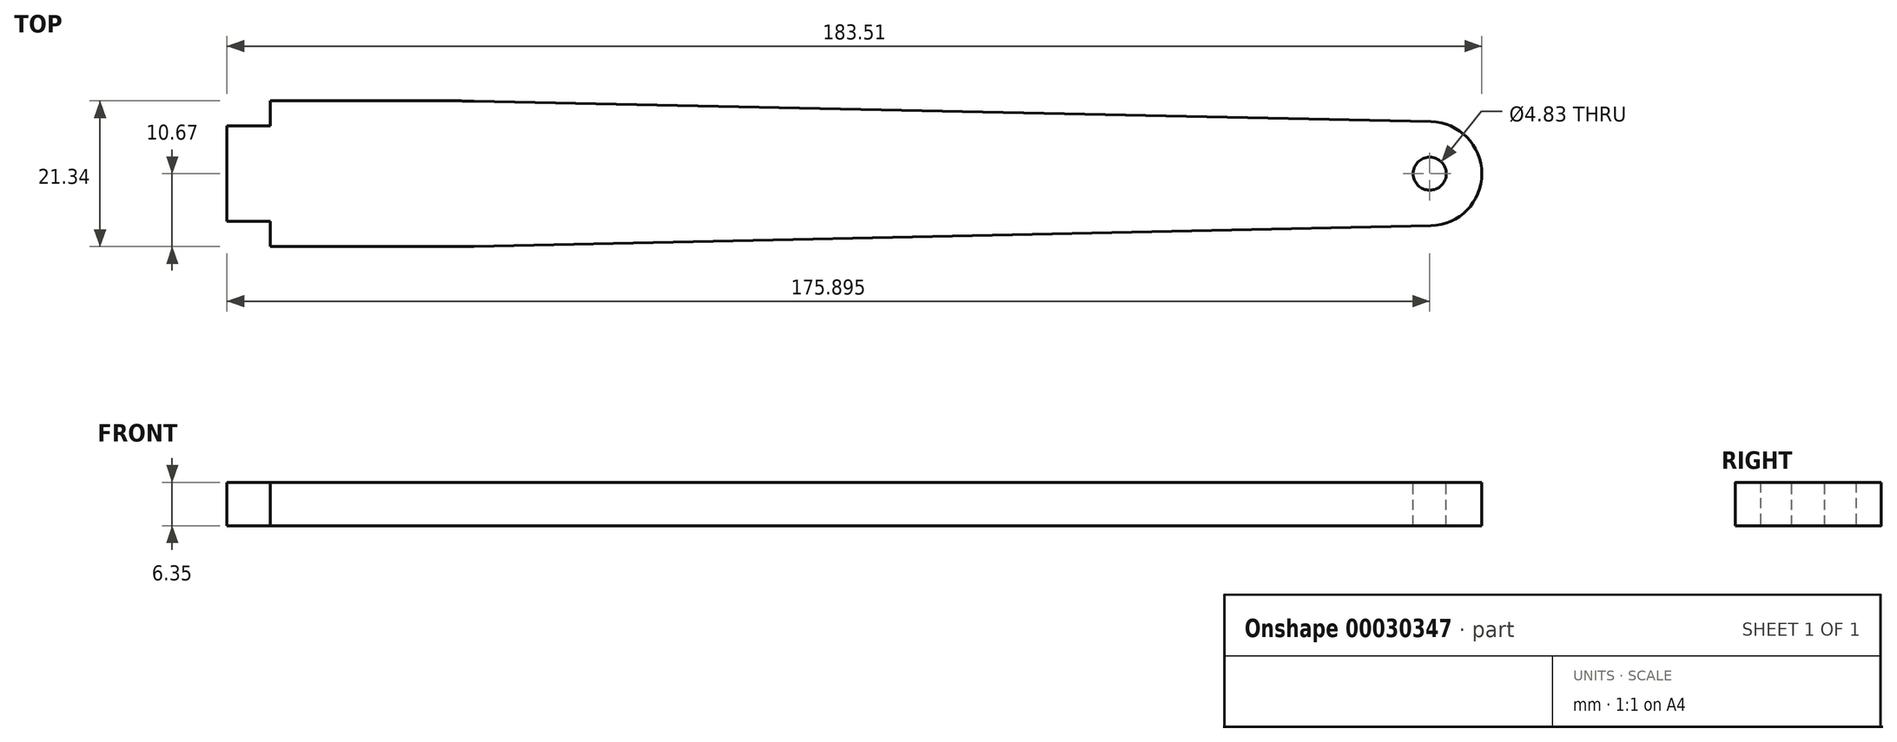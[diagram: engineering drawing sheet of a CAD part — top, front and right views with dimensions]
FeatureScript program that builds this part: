
annotation { "Feature Type Name" : "Feature", "Feature Type Description" : "" }
export const myFeature = defineFeature(function(context is Context, id is Id, definition is map)
    precondition{}
    {
        {
            var Q0;
            Q0=qCreatedBy(makeId("Top.planeOp"),FACE);
            var sketch = newSketch(context, id + "F0", { "sketchPlane" : qUnion([Q0])});
            skLineSegment(sketch, "E0", {"start": v(-6.35, 0) * mm, "end": v(-6.35, 6.99) * mm});
            skLineSegment(sketch, "E1", {"start": v(-6.35, 6.99) * mm, "end": v(0, 6.99) * mm});
            skLineSegment(sketch, "E2", {"start": v(0, 6.99) * mm, "end": v(0, 10.67) * mm});
            skLineSegment(sketch, "E3", {"start": v(0, 10.67) * mm, "end": v(25.4, 10.67) * mm});
            skLineSegment(sketch, "E4", {"start": v(29.76, 10.62) * mm, "end": v(169.7, 7.62) * mm});
            skArc(sketch, "E5", {"start": v(169.7, 7.62) * mm, "mid": v(175, 5.33) * mm, "end": v(177.16, 0) * mm});
            skPoint(sketch, "E6.visualSharp", {"position": v(27.58, 10.67) * mm});
            skArc(sketch, "E6.filletArc", {"start": v(29.76, 10.62) * mm, "mid": v(27.58, 10.66) * mm, "end": v(25.4, 10.67) * mm});
            skArc(sketch, "E7.MirrorCS", {"start": v(169.7, -7.62) * mm, "mid": v(175, -5.33) * mm, "end": v(177.16, 0) * mm});
            skLineSegment(sketch, "E8.MirrorCS", {"start": v(29.76, -10.62) * mm, "end": v(169.7, -7.62) * mm});
            skArc(sketch, "E9.MirrorCS", {"start": v(29.76, -10.62) * mm, "mid": v(27.58, -10.66) * mm, "end": v(25.4, -10.67) * mm});
            skLineSegment(sketch, "E10.MirrorCS", {"start": v(0, -10.67) * mm, "end": v(25.4, -10.67) * mm});
            skLineSegment(sketch, "E11.MirrorCS", {"start": v(0, -6.99) * mm, "end": v(0, -10.67) * mm});
            skLineSegment(sketch, "E12.MirrorCS", {"start": v(-6.35, 0) * mm, "end": v(-6.35, -6.99) * mm});
            skLineSegment(sketch, "E13.MirrorCS", {"start": v(-6.35, -6.99) * mm, "end": v(0, -6.99) * mm});
            skSolve(sketch);
        }
        {
            var Q0;
            Q0 = qSketchRegion(id + "F0", true);
            extrude(context, id + "F1", {"entities" : qUnion([Q0]), "depth" : 6.35 * mm});
        }
        {
            var Q0;
            Q0=makeQuery(id+"F1.opExtrude","CAP_FACE",FACE,{"disambiguationData":[OSD([sQuery(id+"F0.wireOp",EDGE,"E0"),sQuery(id+"F0.wireOp",EDGE,"E1"),sQuery(id+"F0.wireOp",EDGE,"E2"),sQuery(id+"F0.wireOp",EDGE,"E3"),sQuery(id+"F0.wireOp",EDGE,"E4"),sQuery(id+"F0.wireOp",EDGE,"E5"),sQuery(id+"F0.wireOp",EDGE,"E6.filletArc"),sQuery(id+"F0.wireOp",EDGE,"E7.MirrorCS"),sQuery(id+"F0.wireOp",EDGE,"E8.MirrorCS"),sQuery(id+"F0.wireOp",EDGE,"E9.MirrorCS"),sQuery(id+"F0.wireOp",EDGE,"E10.MirrorCS"),sQuery(id+"F0.wireOp",EDGE,"E11.MirrorCS"),sQuery(id+"F0.wireOp",EDGE,"E12.MirrorCS"),sQuery(id+"F0.wireOp",EDGE,"E13.MirrorCS")])],"isStart":false});
            var sketch = newSketch(context, id + "F2", { "sketchPlane" : qUnion([Q0])});
            skCircle(sketch, "E14", {"center": v(169.54, 0) * mm, "radius": 2.41 * mm});
            skSolve(sketch);
        }
        {
            var Q0;
            Q0 = qSketchRegion(id + "F2", true);
            extrude(context, id + "F3", {"entities" : qUnion([Q0]), "operationType" : NewBodyOperationType.REMOVE, "endBound" : BoundingType.THROUGH_ALL, "oppositeDirection" : true, "depth" : 25.4 * mm});
        }
    });
